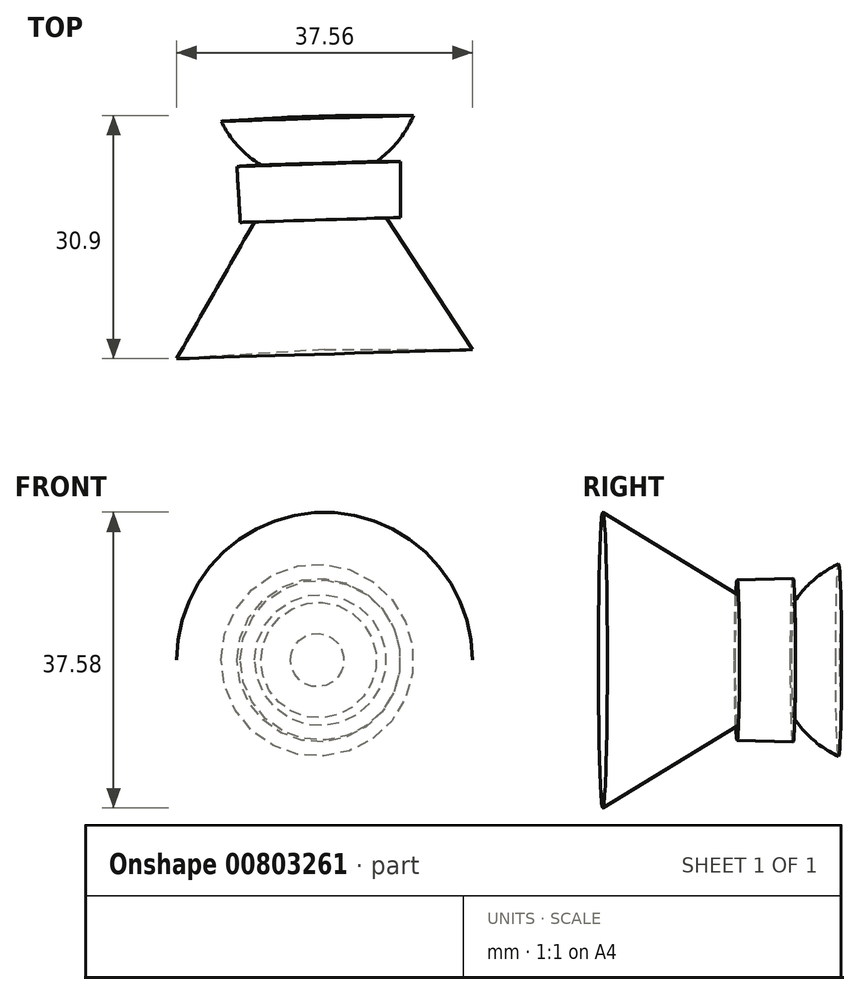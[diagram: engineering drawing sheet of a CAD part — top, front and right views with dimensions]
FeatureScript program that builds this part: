
annotation { "Feature Type Name" : "Feature", "Feature Type Description" : "" }
export const myFeature = defineFeature(function(context is Context, id is Id, definition is map)
    precondition{}
    {
        {
            var Q0;
            Q0=qCreatedBy(makeId("Top.planeOp"),FACE);
            var sketch = newSketch(context, id + "F0", { "sketchPlane" : qUnion([Q0])});
            skLineSegment(sketch, "E0", {"start": v(0, 75) * mm, "end": v(0, -76.65) * mm, "construction": true});
            skArc(sketch, "E1", {"start": v(3.86, 38.5) * mm, "mid": v(9.5, 48.01) * mm, "end": v(0, 53.66) * mm});
            skLineSegment(sketch, "E2.bottom", {"start": v(3.86, 38.5) * mm, "end": v(12.68, 38.5) * mm});
            skLineSegment(sketch, "E2.left", {"start": v(0, 38.5) * mm, "end": v(0, 30.11) * mm});
            skArc(sketch, "E3", {"start": v(8, 32.67) * mm, "mid": v(10.74, 35.26) * mm, "end": v(12.68, 38.5) * mm});
            skLineSegment(sketch, "E4.bottom", {"start": v(8, 32.67) * mm, "end": v(11.04, 32.67) * mm});
            skLineSegment(sketch, "E4.top", {"start": v(9.22, 25.55) * mm, "end": v(11.04, 25.55) * mm});
            skLineSegment(sketch, "E4.left", {"start": v(0, 32.67) * mm, "end": v(0, 25.55) * mm});
            skLineSegment(sketch, "E4.right", {"start": v(11.04, 32.67) * mm, "end": v(11.04, 25.55) * mm});
            skLineSegment(sketch, "E5", {"start": v(9.22, 25.55) * mm, "end": v(20.17, 8.76) * mm});
            skLineSegment(sketch, "E6", {"start": v(20.17, 8.76) * mm, "end": v(1.37, 8.76) * mm});
            skLineSegment(sketch, "E7", {"start": v(0, 53.66) * mm, "end": v(1.37, 8.76) * mm});
            skSolve(sketch);
        }
        {
            var Q0;
            Q0=makeQuery(id+"F0.imprint","IMPRINT",FACE,{"disambiguationData":[TD([[makeQuery(id+"F0.imprint","IMPRINT",EDGE,{"derivedFrom":sQuery(id+"F0.wireOp",EDGE,"E1")}),1.0]])]});
            var Q1;
            Q1=sQuery(id+"F0.wireOp",EDGE,"E7");
            revolve(context, id + "F1", {"surfaceOperationType" : NewSurfaceOperationType.NEW, "entities" : qUnion([Q0]), "axis" : qUnion([Q1]), "revolveType" : RevolveType.FULL});
        }
    });
